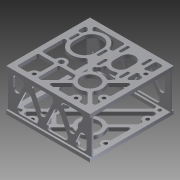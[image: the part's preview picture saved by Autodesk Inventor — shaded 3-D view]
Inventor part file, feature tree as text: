
AUTODESK INVENTOR PART (.ipt)
format: ipt  version: 2012 (Build 160160000, 160)  size: 897,024 bytes
history: native  units: in
note: dims shown in document units (in); Inventor stores cm internally (conversion verified against a paired STEP export)
features: thread x8, extrude x7, sketch x5, fillet x3, projected_geometry x1
ambient origin geometry x8: Origin, YZ Plane, XZ Plane, XY Plane, X Axis, Y Axis, Z Axis, Center Point
bodies: Solid1 (feature_tree)
feature tree (24):
  extrude  "Extrusion1"  Depth=0.1875in
  sketch  "Sketch2"  dims[d4=0.25in d5=0.25in d6=6.0in d7=0.0in]
  extrude  "Extrusion2"  Depth=6.0in TaperAngle=0.0deg
  extrude  "Extrusion3"  Depth=1.25in
  extrude  "Extrusion4"  Depth=1.625in
  fillet  "Fillet2"  Radius=0.375in
  sketch  "Sketch6"  dims[d20=0.25in d21=0.125in d22=0.25in d24=0.25in d25=0.125in d27=0.125in d32=0.25in d33=0.0in d35=0.375in d36=0.375in d37=0.375in d38=0.375in d39=0.1719in d40=0.3438in d41=0.3438in d42=0.3438in d43=0.3438in d44=0.125in d46=0.125in d49=0.125in d50=0.125in d51=0.125in d52=0.125in d53=0.125in d54=0.125in d55=0.125in d56=0.125in d57=0.25in d58=0.0in d60=0.3798in d61=0.287in d62=0.287in d63=0.287in d64=0.125in d65=0.125in d66=0.125in d67=0.125in d68=0.125in d69=0.125in d70=0.125in d71=0.125in d72=0.125in d73=0.125in d74=0.375in d76=0.25in d77=0.375in d78=0.375in d79=0.25in d80=0.0in d81=0.25in d88=0.125in d89=1.25in d90=1.5in d91=0.75in d92=0.5in d94=0.2in d96=0.9in d97=1.0in d98=0.5in d99=0.5in d101=2.0in d102=0.2in d103=0.8in d104=0.8in d105=0.7874in d107=1.6in d108=0.7874in d110=1.6in d114=1.0in d115=1.0in d116=1.625in d117=1.0in d119=0.2in d122=4.5in d123=1.3125in d124=0.366in d126=2.3in d127=0.25in d128=0.0in d129=0.375in d131=4.5in d132=0.125in d153=0.25in d154=0.125in d156=0.375in d157=0.375in d160=0.25in d161=0.125in d162=0.25in d163=0.125in d165=0.875in d166=0.125in d168=0.375in d169=0.25in d170=0.125in d171=1.0in d172=0.25in d177=0.125in d178=0.6in d179=0.25in d180=0.0in d181=0.125in d183=0.25in d185=0.25in d186=0.125in d188=1.5625in d190=1.3125in d191=0.366in d193=0.25in d194=0.125in d197=1.0in d198=1.176in d199=0.1in d200=0.0in d201=0.125in d203=0.25in d204=0.25in d205=0.125in d207=2.1875in d208=2.0312in d211=0.125in d212=0.3in d213=0.5in d214=0.25in d215=0.3125in d220=0.5in d221=1.5in d222=0.25in d224=0.1875in d225=2.3in d226=0.35in d227=0.25in d228=1.5in d229=1.5in d230=0.5821in d231=0.25in d232=1.5in d233=0.125in d234=0.25in d235=2.0in d236=0.25in d237=1.5in d238=0.3125in d239=0.7874in d241=3.0in d242=0.3937in d244=1.0in d246=1.5in d247=0.7874in d249=3.0in d250=0.3937in d252=1.0in d254=0.5in d255=0.25in d256=0.3125in d257=0.25in d258=0.5in d259=0.3125in d260=0.25in d262=0.75in d264=6.0in d267=0.25in d269=3.0in d270=6.0in d272=0.25in d273=0.125in d274=0.125in d275=0.1435in d276=2.0in d277=1.0in d278=0.0in d279=1.0in d280=0.0in d281=1.0in d282=0.0in d283=1.0in d284=0.0in d285=1.0in d286=0.0in d287=1.0in d288=0.0in d289=1.0in d290=0.0in d291=1.0in d292=0.0in]
  fillet  "Fillet3"  Radius=0.875in
  extrude  "Extrusion5"  Depth=0.125in
  extrude  "Extrusion6"  Depth=0.25in
  fillet  "Fillet4"  Radius=0.25in
  extrude  "Extrusion7"  Depth=0.125in
  thread  "Thread1"  [1 undecoded]
  thread  "Thread2"  [1 undecoded]
  thread  "Thread3"  [1 undecoded]
  thread  "Thread4"  [1 undecoded]
  thread  "Thread5"  [1 undecoded]
  thread  "Thread6"  [1 undecoded]
  thread  "Thread7"  [1 undecoded]
  thread  "Thread8"  [1 undecoded]
  sketch  "Sketch1"  dims[d1=3.0in d2=0.1875in d3=0.25in]
  sketch  "Sketch4"  dims[d11=2.0312in d13=1.25in]
  sketch  "Sketch5"  dims[d15=2.625in d16=1.625in d18=0.375in d19=0.875in]
  projected_geometry  "Projected Loop1"
note: 8 required parameter values undecoded (feature->parameter linkage not recoverable at this tier; creation-order binding heuristic only, values carry confidence <= 0.55)
